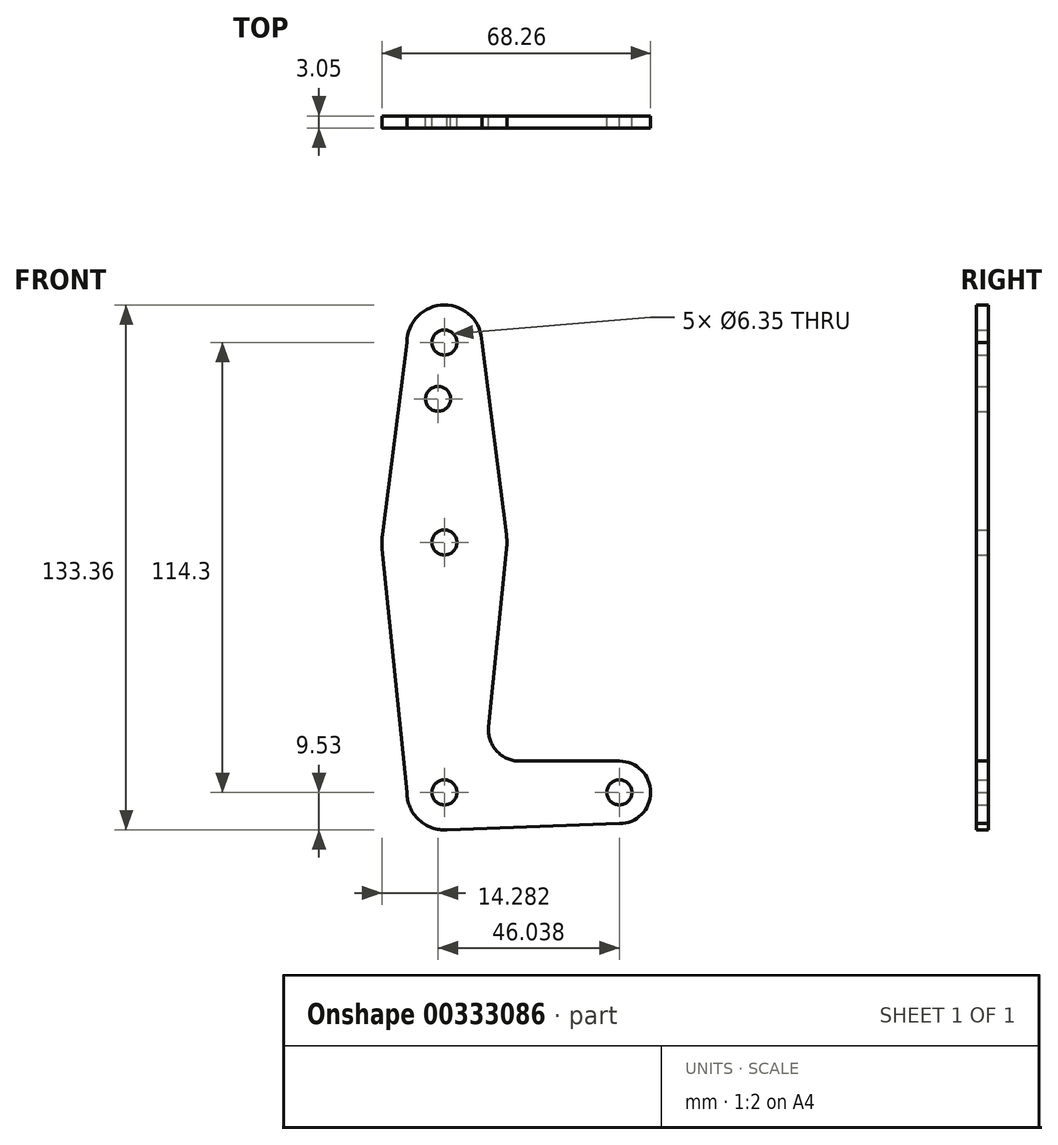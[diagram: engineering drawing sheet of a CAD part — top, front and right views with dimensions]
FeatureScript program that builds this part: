
annotation { "Feature Type Name" : "Feature", "Feature Type Description" : "" }
export const myFeature = defineFeature(function(context is Context, id is Id, definition is map)
    precondition{}
    {
        {
            var Q0;
            Q0=qCreatedBy(makeId("Front.planeOp"),FACE);
            var sketch = newSketch(context, id + "F0", { "sketchPlane" : qUnion([Q0])});
            skLineSegment(sketch, "E0", {"start": v(0, 0) * mm, "end": v(0, 114.3) * mm, "construction": true});
            skLineSegment(sketch, "E1", {"start": v(0, 0) * mm, "end": v(44.45, 0) * mm, "construction": true});
            skCircle(sketch, "E2", {"center": v(0, 0) * mm, "radius": 9.53 * mm});
            skCircle(sketch, "E3", {"center": v(44.45, 0) * mm, "radius": 7.94 * mm});
            skCircle(sketch, "E4", {"center": v(0, 114.3) * mm, "radius": 9.52 * mm});
            skCircle(sketch, "E5", {"center": v(0, 63.5) * mm, "radius": 15.88 * mm});
            skLineSegment(sketch, "E6", {"start": v(-9.52, 114.3) * mm, "end": v(-15.75, 65.5) * mm});
            skLineSegment(sketch, "E7", {"start": v(9.52, 114.3) * mm, "end": v(15.75, 65.5) * mm});
            skLineSegment(sketch, "E8", {"start": v(-9.53, 0) * mm, "end": v(-15.8, 61.9) * mm});
            skLineSegment(sketch, "E9", {"start": v(15.8, 61.9) * mm, "end": v(11.22, 16.69) * mm});
            skLineSegment(sketch, "E10", {"start": v(0, -9.52) * mm, "end": v(44.45, -7.94) * mm});
            skLineSegment(sketch, "E11", {"start": v(19.12, 7.94) * mm, "end": v(44.45, 7.94) * mm});
            skCircle(sketch, "E12", {"center": v(-1.59, 100) * mm, "radius": 3.18 * mm});
            skCircle(sketch, "E13", {"center": v(0, 114.3) * mm, "radius": 3.18 * mm});
            skCircle(sketch, "E14", {"center": v(0, 63.5) * mm, "radius": 3.18 * mm});
            skCircle(sketch, "E15", {"center": v(0, 0) * mm, "radius": 3.18 * mm});
            skCircle(sketch, "E16", {"center": v(44.45, 0) * mm, "radius": 3.18 * mm});
            skArc(sketch, "E17.filletArc", {"start": v(11.22, 16.69) * mm, "mid": v(13.23, 10.56) * mm, "end": v(19.12, 7.94) * mm});
            skSolve(sketch);
        }
        {
            var Q0;
            Q0 = qSketchRegion(id + "F0", true);
            extrude(context, id + "F1", {"entities" : qUnion([Q0]), "depth" : 3.05 * mm});
        }
    });
